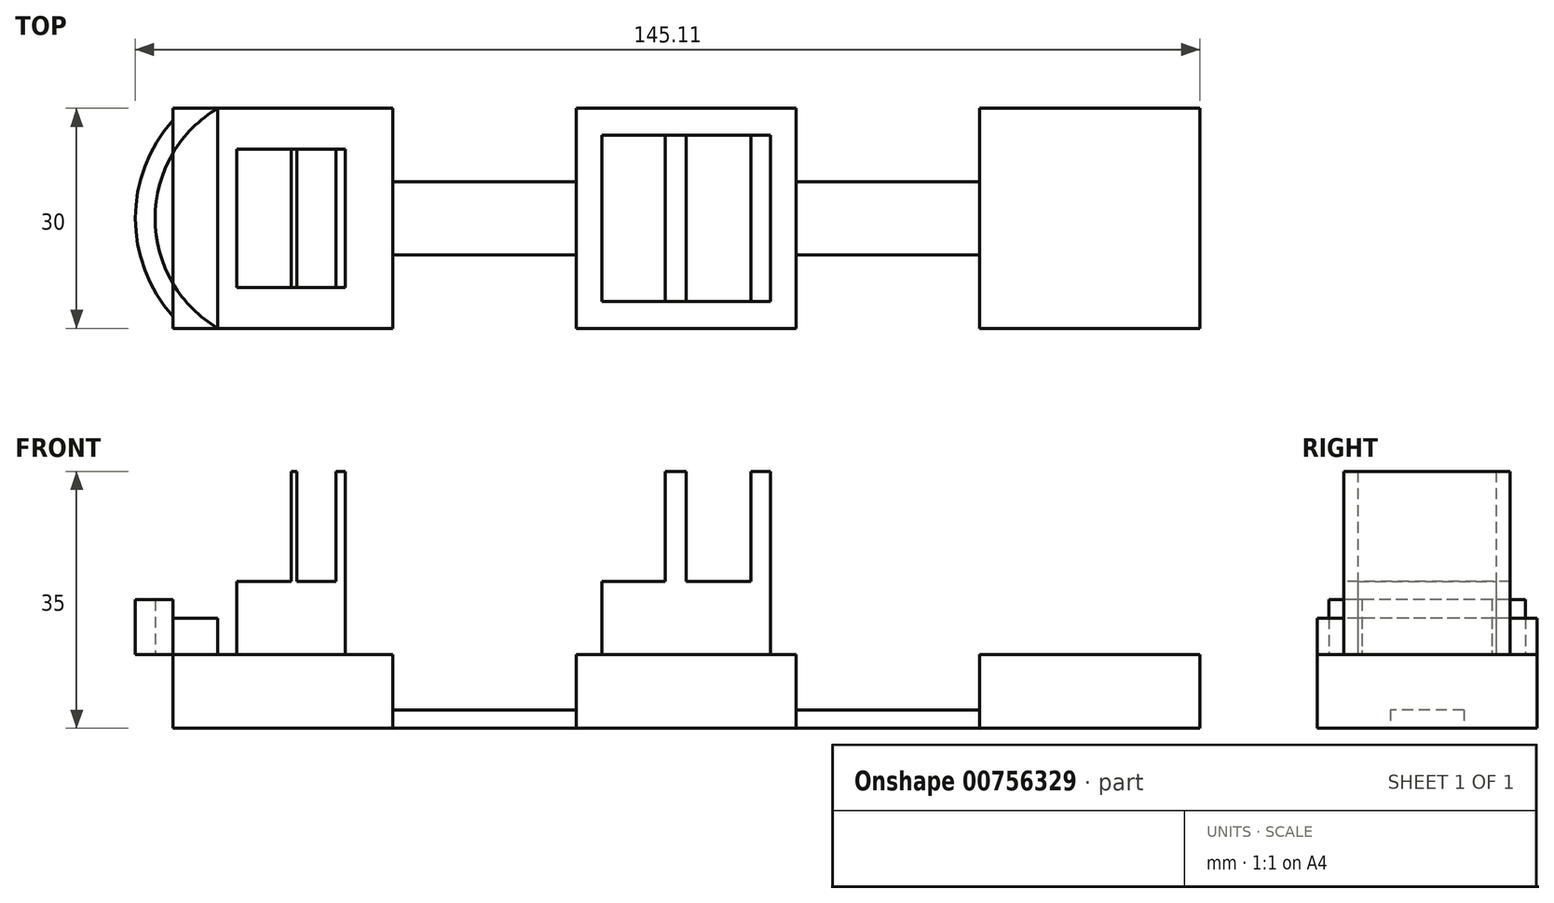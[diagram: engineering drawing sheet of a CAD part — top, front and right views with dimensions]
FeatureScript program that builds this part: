
annotation { "Feature Type Name" : "Feature", "Feature Type Description" : "" }
export const myFeature = defineFeature(function(context is Context, id is Id, definition is map)
    precondition{}
    {
        {
            var Q0;
            Q0=qCreatedBy(makeId("Top.planeOp"),FACE);
            var sketch = newSketch(context, id + "F0", { "sketchPlane" : qUnion([Q0])});
            skLineSegment(sketch, "E0.bottom", {"start": v(15, 15) * mm, "end": v(-15, 15) * mm});
            skLineSegment(sketch, "E0.top", {"start": v(15, -15) * mm, "end": v(-15, -15) * mm});
            skLineSegment(sketch, "E0.left", {"start": v(15, 15) * mm, "end": v(15, -15) * mm});
            skLineSegment(sketch, "E0.right", {"start": v(-15, 15) * mm, "end": v(-15, -15) * mm});
            skPoint(sketch, "E0.middle", {"position": v(0, 0) * mm});
            skLineSegment(sketch, "E1", {"start": v(0, 15) * mm, "end": v(0, -15) * mm});
            skLineSegment(sketch, "E2.bottom", {"start": v(55, 5) * mm, "end": v(-55, 5) * mm});
            skLineSegment(sketch, "E2.top", {"start": v(55, -5) * mm, "end": v(-55, -5) * mm});
            skLineSegment(sketch, "E2.left", {"start": v(55, 5) * mm, "end": v(55, -5) * mm});
            skLineSegment(sketch, "E2.right", {"start": v(-55, 5) * mm, "end": v(-55, -5) * mm});
            skLineSegment(sketch, "E3.bottom", {"start": v(-70, 15) * mm, "end": v(-40, 15) * mm});
            skLineSegment(sketch, "E3.top", {"start": v(-70, -15) * mm, "end": v(-40, -15) * mm});
            skLineSegment(sketch, "E3.left", {"start": v(-70, 15) * mm, "end": v(-70, -15) * mm});
            skLineSegment(sketch, "E3.right", {"start": v(-40, 15) * mm, "end": v(-40, -15) * mm});
            skPoint(sketch, "E3.middle", {"position": v(-55, 0) * mm});
            skLineSegment(sketch, "E4.bottom", {"start": v(70, 15) * mm, "end": v(40, 15) * mm});
            skLineSegment(sketch, "E4.top", {"start": v(70, -15) * mm, "end": v(40, -15) * mm});
            skLineSegment(sketch, "E4.left", {"start": v(70, 15) * mm, "end": v(70, -15) * mm});
            skLineSegment(sketch, "E4.right", {"start": v(40, 15) * mm, "end": v(40, -15) * mm});
            skPoint(sketch, "E4.middle", {"position": v(55, 0) * mm});
            skSolve(sketch);
        }
        {
            var Q0;
            {var subQ1=sQuery(id+"F0.wireOp",EDGE,"E2.right");Q0=makeQuery(id+"F0.imprint","IMPRINT",FACE,{"disambiguationData":[TD([[makeQuery(id+"F0.imprint","IMPRINT",EDGE,{"derivedFrom":subQ1}),-1.0]])]});}
            var Q1;
            {var subQ0=sQuery(id+"F0.wireOp",EDGE,"E0.right");var subQ1=sQuery(id+"F0.wireOp",EDGE,"E0.top");var subQ2=makeQuery(id+"F0.imprint","INTERSECT",VERTEX,{"derivedFrom":[subQ1,subQ0]});Q1=makeQuery(id+"F0.imprint","IMPRINT",FACE,{"disambiguationData":[TD([[makeQuery(id+"F0.imprint","IMPRINT",EDGE,{"disambiguationData":[TD([[subQ2,1.0]])],"derivedFrom":subQ1}),-1.0]])]});}
            var Q2;
            {var subQ0=sQuery(id+"F0.wireOp",EDGE,"E0.right");var subQ1=sQuery(id+"F0.wireOp",EDGE,"E0.bottom");var subQ2=makeQuery(id+"F0.imprint","INTERSECT",VERTEX,{"derivedFrom":[subQ1,subQ0]});Q2=makeQuery(id+"F0.imprint","IMPRINT",FACE,{"disambiguationData":[TD([[makeQuery(id+"F0.imprint","IMPRINT",EDGE,{"disambiguationData":[TD([[subQ2,1.0]])],"derivedFrom":subQ1}),1.0]])]});}
            var Q3;
            {var subQ0=sQuery(id+"F0.wireOp",EDGE,"E0.left");var subQ1=sQuery(id+"F0.wireOp",EDGE,"E0.bottom");var subQ2=makeQuery(id+"F0.imprint","INTERSECT",VERTEX,{"derivedFrom":[subQ1,subQ0]});Q3=makeQuery(id+"F0.imprint","IMPRINT",FACE,{"disambiguationData":[TD([[makeQuery(id+"F0.imprint","IMPRINT",EDGE,{"disambiguationData":[TD([[subQ2,-1.0]])],"derivedFrom":subQ1}),1.0]])]});}
            var Q4;
            {var subQ0=sQuery(id+"F0.wireOp",EDGE,"E0.left");var subQ1=sQuery(id+"F0.wireOp",EDGE,"E0.top");var subQ2=makeQuery(id+"F0.imprint","INTERSECT",VERTEX,{"derivedFrom":[subQ1,subQ0]});Q4=makeQuery(id+"F0.imprint","IMPRINT",FACE,{"disambiguationData":[TD([[makeQuery(id+"F0.imprint","IMPRINT",EDGE,{"disambiguationData":[TD([[subQ2,-1.0]])],"derivedFrom":subQ1}),-1.0]])]});}
            var Q5;
            {var subQ0=sQuery(id+"F0.wireOp",EDGE,"E2.bottom");var subQ1=sQuery(id+"F0.wireOp",EDGE,"E0.right");var subQ2=makeQuery(id+"F0.imprint","INTERSECT",VERTEX,{"derivedFrom":[subQ1,subQ0]});Q5=makeQuery(id+"F0.imprint","IMPRINT",FACE,{"disambiguationData":[TD([[makeQuery(id+"F0.imprint","IMPRINT",EDGE,{"disambiguationData":[TD([[subQ2,-1.0]])],"derivedFrom":subQ1}),1.0]])]});}
            var Q6;
            {var subQ0=sQuery(id+"F0.wireOp",EDGE,"E2.bottom");var subQ1=sQuery(id+"F0.wireOp",EDGE,"E0.left");var subQ2=makeQuery(id+"F0.imprint","INTERSECT",VERTEX,{"derivedFrom":[subQ1,subQ0]});Q6=makeQuery(id+"F0.imprint","IMPRINT",FACE,{"disambiguationData":[TD([[makeQuery(id+"F0.imprint","IMPRINT",EDGE,{"disambiguationData":[TD([[subQ2,-1.0]])],"derivedFrom":subQ1}),-1.0]])]});}
            var Q7;
            {var subQ0=sQuery(id+"F0.wireOp",EDGE,"E2.left");Q7=makeQuery(id+"F0.imprint","IMPRINT",FACE,{"disambiguationData":[TD([[makeQuery(id+"F0.imprint","IMPRINT",EDGE,{"derivedFrom":subQ0}),1.0]])]});}
            var Q8;
            {var subQ0=sQuery(id+"F0.wireOp",EDGE,"E2.right");Q8=makeQuery(id+"F0.imprint","IMPRINT",FACE,{"disambiguationData":[TD([[makeQuery(id+"F0.imprint","IMPRINT",EDGE,{"derivedFrom":subQ0}),1.0]])]});}
            var Q9;
            {var subQ0=sQuery(id+"F0.wireOp",EDGE,"E2.left");Q9=makeQuery(id+"F0.imprint","IMPRINT",FACE,{"disambiguationData":[TD([[makeQuery(id+"F0.imprint","IMPRINT",EDGE,{"derivedFrom":subQ0}),-1.0]])]});}
            extrude(context, id + "F1", {"entities" : qUnion([Q0, Q1, Q2, Q3, Q4, Q5, Q6, Q7, Q8, Q9]), "depth" : 10 * mm, "offsetDistance" : 25 * mm});
        }
        {
            var Q0;
            {var subQ0=sQuery(id+"F0.wireOp",EDGE,"E2.bottom");var subQ1=sQuery(id+"F0.wireOp",EDGE,"E0.right");var subQ2=makeQuery(id+"F0.imprint","INTERSECT",VERTEX,{"derivedFrom":[subQ1,subQ0]});Q0=makeQuery(id+"F0.imprint","IMPRINT",FACE,{"disambiguationData":[TD([[makeQuery(id+"F0.imprint","IMPRINT",EDGE,{"disambiguationData":[TD([[subQ2,-1.0]])],"derivedFrom":subQ1}),-1.0]])]});}
            var Q1;
            {var subQ0=sQuery(id+"F0.wireOp",EDGE,"E2.bottom");var subQ1=sQuery(id+"F0.wireOp",EDGE,"E0.left");var subQ2=makeQuery(id+"F0.imprint","INTERSECT",VERTEX,{"derivedFrom":[subQ1,subQ0]});Q1=makeQuery(id+"F0.imprint","IMPRINT",FACE,{"disambiguationData":[TD([[makeQuery(id+"F0.imprint","IMPRINT",EDGE,{"disambiguationData":[TD([[subQ2,-1.0]])],"derivedFrom":subQ1}),1.0]])]});}
            extrude(context, id + "F2", {"entities" : qUnion([Q0, Q1]), "depth" : 2.5 * mm, "offsetDistance" : 25 * mm});
        }
        {
            var Q0;
            Q0=makeQuery(id+"F1.opExtrude","CAP_FACE",FACE,{"disambiguationData":[OSD([sQuery(id+"F0.wireOp",EDGE,"E3.bottom"),sQuery(id+"F0.wireOp",EDGE,"E3.top"),sQuery(id+"F0.wireOp",EDGE,"E3.left"),sQuery(id+"F0.wireOp",EDGE,"E3.right")])],"isStart":false});
            var sketch = newSketch(context, id + "F3", { "sketchPlane" : qUnion([Q0])});
            skCircle(sketch, "E5", {"center": v(-55, 0) * mm, "radius": 20.1 * mm});
            skPoint(sketch, "E5.centerSnap0", {"position": v(-55, 15) * mm});
            skPoint(sketch, "E5.centerSnap1", {"position": v(-40, 0) * mm});
            skCircle(sketch, "E6", {"center": v(-55, 0) * mm, "radius": 17.43 * mm});
            skLineSegment(sketch, "E7", {"start": v(-63.87, 15) * mm, "end": v(-63.87, -15) * mm});
            skSolve(sketch);
        }
        {
            var Q0;
            {var subQ0=sQuery(id+"F3.wireOp",EDGE,"E7");Q0=makeQuery(id+"F3.imprint","IMPRINT",FACE,{"disambiguationData":[TD([[makeQuery(id+"F3.imprint","IMPRINT",EDGE,{"derivedFrom":subQ0}),-1.0]])]});}
            extrude(context, id + "F4", {"entities" : qUnion([Q0]), "operationType" : NewBodyOperationType.ADD, "depth" : 5 * mm, "offsetDistance" : 25 * mm});
        }
        {
            var Q0;
            {var subQ0=sQuery(id+"F3.wireOp",EDGE,"E5");var subQ1=makeQuery(id+"F1.opExtrude","CAP_EDGE",EDGE,{"disambiguationData":[OSD([sQuery(id+"F0.wireOp",EDGE,"E3.left")])],"isStart":false});var subQ2=makeQuery(id+"F3.imprint","INTERSECT",VERTEX,{"disambiguationData":[OD(0.0)],"derivedFrom":[subQ1,subQ0]});Q0=makeQuery(id+"F3.imprint","IMPRINT",FACE,{"disambiguationData":[TD([[makeQuery(id+"F3.imprint","IMPRINT",EDGE,{"disambiguationData":[TD([[subQ2,-1.0]])],"derivedFrom":subQ0}),1.0]])]});}
            extrude(context, id + "F5", {"entities" : qUnion([Q0]), "depth" : 7.5 * mm, "offsetDistance" : 25 * mm});
        }
        {
            var Q0;
            {var subQ0=sQuery(id+"F0.wireOp",EDGE,"E3.top");var subQ1=sQuery(id+"F3.wireOp",EDGE,"E7");var subQ2=sQuery(id+"F0.wireOp",EDGE,"E3.right");var subQ3=sQuery(id+"F0.wireOp",EDGE,"E3.left");var subQ4=sQuery(id+"F0.wireOp",EDGE,"E3.bottom");var subQ5=makeQuery(id+"F1.opExtrude","CAP_FACE",FACE,{"disambiguationData":[OSD([subQ4,subQ0,subQ3,subQ2])],"isStart":false});var subQ6=sQuery(id+"F3.wireOp",EDGE,"E6");var subQ7=makeQuery(id+"F1.opExtrude","CAP_EDGE",EDGE,{"disambiguationData":[OSD([subQ3])],"isStart":false});Q0=makeQuery(id+"F4.boolean.opBoolean","SPLIT",FACE,{"disambiguationData":[TD([makeQuery(id+"F1.opExtrude","SWEPT_FACE",FACE,{"disambiguationData":[OSD([subQ4])]}),subQ5,makeQuery(id+"F1.opExtrude","SWEPT_FACE",FACE,{"disambiguationData":[OSD([subQ0])]}),makeQuery(id+"F1.opExtrude","SWEPT_FACE",FACE,{"disambiguationData":[OSD([subQ2])]}),makeQuery(id+"F4.opExtrude","SWEPT_FACE",FACE,{"disambiguationData":[OSD([subQ6]),TDD([makeQuery(id+"F3.imprint","IMPRINT",EDGE,{"disambiguationData":[TD([[makeQuery(id+"F3.imprint","INTERSECT",VERTEX,{"disambiguationData":[OD(0.0)],"derivedFrom":[subQ7,subQ6]}),1.0]])],"derivedFrom":subQ6})])]}),makeQuery(id+"F4.opExtrude","SWEPT_FACE",FACE,{"disambiguationData":[OSD([subQ6]),TDD([makeQuery(id+"F3.imprint","IMPRINT",EDGE,{"disambiguationData":[TD([[makeQuery(id+"F3.imprint","INTERSECT",VERTEX,{"disambiguationData":[OD(1.0)],"derivedFrom":[subQ7,subQ6]}),-1.0]])],"derivedFrom":subQ6})])]}),makeQuery(id+"F4.opExtrude","SWEPT_FACE",FACE,{"disambiguationData":[OSD([subQ1])]})])],"derivedFrom":subQ5});}
            var sketch = newSketch(context, id + "F6", { "sketchPlane" : qUnion([Q0])});
            skLineSegment(sketch, "E8.bottom", {"start": v(-46.49, 9.43) * mm, "end": v(-61.28, 9.43) * mm});
            skLineSegment(sketch, "E8.top", {"start": v(-46.49, -9.43) * mm, "end": v(-61.28, -9.43) * mm});
            skLineSegment(sketch, "E8.left", {"start": v(-46.49, 9.43) * mm, "end": v(-46.49, -9.43) * mm});
            skLineSegment(sketch, "E8.right", {"start": v(-61.28, 9.43) * mm, "end": v(-61.28, -9.43) * mm});
            skPoint(sketch, "E8.middle", {"position": v(-53.88, 0) * mm});
            skLineSegment(sketch, "E9", {"start": v(-53.88, -9.43) * mm, "end": v(-53.88, 9.43) * mm});
            skLineSegment(sketch, "E10", {"start": v(-53.07, -9.43) * mm, "end": v(-53.07, 9.43) * mm});
            skLineSegment(sketch, "E11", {"start": v(-47.77, -9.43) * mm, "end": v(-47.77, 9.43) * mm});
            skSolve(sketch);
        }
        {
            var Q0;
            {var subQ0=sQuery(id+"F6.wireOp",EDGE,"E9");Q0=makeQuery(id+"F6.imprint","IMPRINT",FACE,{"disambiguationData":[TD([[makeQuery(id+"F6.imprint","IMPRINT",EDGE,{"derivedFrom":subQ0}),-1.0]])]});}
            var Q1;
            {var subQ0=sQuery(id+"F6.wireOp",EDGE,"E8.left");Q1=makeQuery(id+"F6.imprint","IMPRINT",FACE,{"disambiguationData":[TD([[makeQuery(id+"F6.imprint","IMPRINT",EDGE,{"derivedFrom":subQ0}),-1.0]])]});}
            extrude(context, id + "F7", {"entities" : qUnion([Q0, Q1]), "operationType" : NewBodyOperationType.ADD, "depth" : 25 * mm, "offsetDistance" : 25 * mm});
        }
        {
            var Q0;
            {var subQ0=sQuery(id+"F6.wireOp",EDGE,"E8.right");Q0=makeQuery(id+"F6.imprint","IMPRINT",FACE,{"disambiguationData":[TD([[makeQuery(id+"F6.imprint","IMPRINT",EDGE,{"derivedFrom":subQ0}),1.0]])]});}
            var Q1;
            {var subQ0=sQuery(id+"F6.wireOp",EDGE,"E10");Q1=makeQuery(id+"F6.imprint","IMPRINT",FACE,{"disambiguationData":[TD([[makeQuery(id+"F6.imprint","IMPRINT",EDGE,{"derivedFrom":subQ0}),-1.0]])]});}
            extrude(context, id + "F8", {"entities" : qUnion([Q0, Q1]), "operationType" : NewBodyOperationType.ADD, "depth" : 10 * mm, "offsetDistance" : 25 * mm});
        }
        {
            var Q0;
            Q0=makeQuery(id+"F1.opExtrude","CAP_FACE",FACE,{"disambiguationData":[OSD([sQuery(id+"F0.wireOp",EDGE,"E0.bottom"),sQuery(id+"F0.wireOp",EDGE,"E0.top"),sQuery(id+"F0.wireOp",EDGE,"E0.left"),sQuery(id+"F0.wireOp",EDGE,"E0.right")])],"isStart":false});
            var sketch = newSketch(context, id + "F9", { "sketchPlane" : qUnion([Q0])});
            skLineSegment(sketch, "E12.bottom", {"start": v(-11.5, 11.33) * mm, "end": v(11.5, 11.33) * mm});
            skLineSegment(sketch, "E12.top", {"start": v(-11.5, -11.33) * mm, "end": v(11.5, -11.33) * mm});
            skLineSegment(sketch, "E12.left", {"start": v(-11.5, 11.33) * mm, "end": v(-11.5, -11.33) * mm});
            skLineSegment(sketch, "E12.right", {"start": v(11.5, 11.33) * mm, "end": v(11.5, -11.33) * mm});
            skPoint(sketch, "E12.middle", {"position": v(0, 0) * mm});
            skLineSegment(sketch, "E13", {"start": v(-2.86, 11.33) * mm, "end": v(-2.86, -11.33) * mm});
            skLineSegment(sketch, "E14", {"start": v(-2.86, -11.33) * mm, "end": v(0, -11.33) * mm});
            skLineSegment(sketch, "E15", {"start": v(0, -11.33) * mm, "end": v(0, 11.33) * mm});
            skLineSegment(sketch, "E16", {"start": v(8.83, 11.33) * mm, "end": v(8.83, -11.33) * mm});
            skSolve(sketch);
        }
        {
            var Q0;
            {var subQ0=sQuery(id+"F9.wireOp",EDGE,"E13");Q0=makeQuery(id+"F9.imprint","IMPRINT",FACE,{"disambiguationData":[TD([[makeQuery(id+"F9.imprint","IMPRINT",EDGE,{"derivedFrom":subQ0}),1.0]])]});}
            var Q1;
            {var subQ0=sQuery(id+"F9.wireOp",EDGE,"E12.right");Q1=makeQuery(id+"F9.imprint","IMPRINT",FACE,{"disambiguationData":[TD([[makeQuery(id+"F9.imprint","IMPRINT",EDGE,{"derivedFrom":subQ0}),-1.0]])]});}
            extrude(context, id + "F10", {"entities" : qUnion([Q0, Q1]), "operationType" : NewBodyOperationType.ADD, "depth" : 25 * mm, "offsetDistance" : 25 * mm});
        }
        {
            var Q0;
            {var subQ0=sQuery(id+"F9.wireOp",EDGE,"E12.left");Q0=makeQuery(id+"F9.imprint","IMPRINT",FACE,{"disambiguationData":[TD([[makeQuery(id+"F9.imprint","IMPRINT",EDGE,{"derivedFrom":subQ0}),1.0]])]});}
            var Q1;
            {var subQ0=sQuery(id+"F9.wireOp",EDGE,"E15");Q1=makeQuery(id+"F9.imprint","IMPRINT",FACE,{"disambiguationData":[TD([[makeQuery(id+"F9.imprint","IMPRINT",EDGE,{"derivedFrom":subQ0}),-1.0]])]});}
            extrude(context, id + "F11", {"entities" : qUnion([Q0, Q1]), "operationType" : NewBodyOperationType.ADD, "depth" : 10 * mm, "offsetDistance" : 25 * mm});
        }
    });
